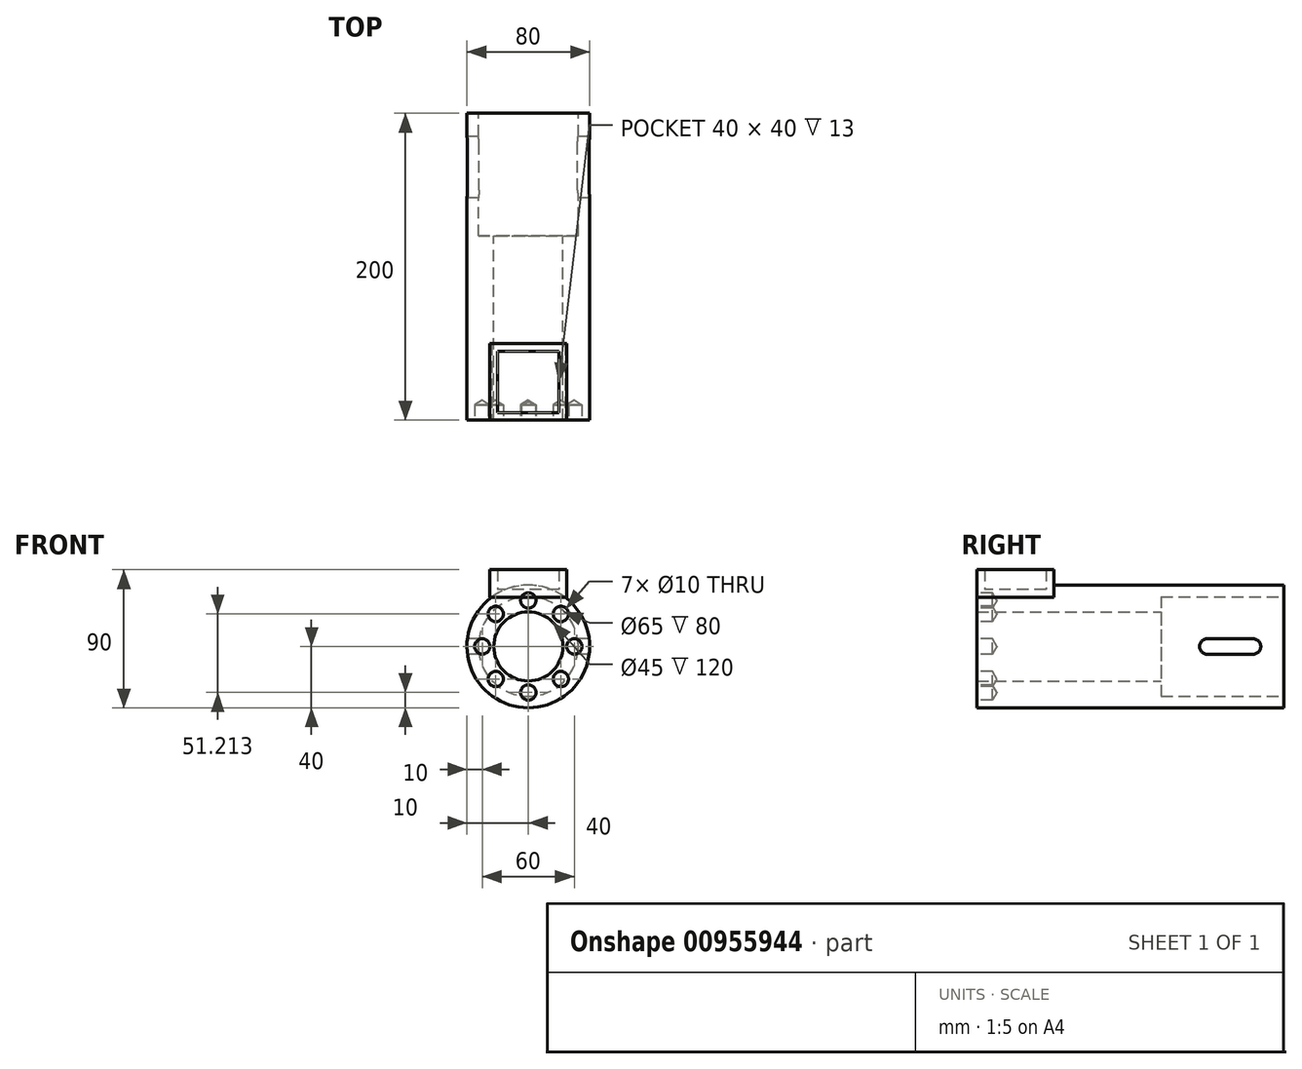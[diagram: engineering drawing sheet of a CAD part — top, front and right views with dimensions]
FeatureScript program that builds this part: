
annotation { "Feature Type Name" : "Feature", "Feature Type Description" : "" }
export const myFeature = defineFeature(function(context is Context, id is Id, definition is map)
    precondition{}
    {
        {
            var Q0;
            Q0=qCreatedBy(makeId("Front.planeOp"),FACE);
            var sketch = newSketch(context, id + "F0", { "sketchPlane" : qUnion([Q0])});
            skLineSegment(sketch, "E0", {"start": v(0, 0) * mm, "end": v(0, -32) * mm});
            skCircle(sketch, "E1", {"center": v(0, -32) * mm, "radius": 40 * mm});
            skSolve(sketch);
        }
        {
            var Q0;
            Q0=makeQuery(id+"F0.imprint","IMPRINT",FACE,{"disambiguationData":[TD([[makeQuery(id+"F0.imprint","IMPRINT",EDGE,{"derivedFrom":sQuery(id+"F0.wireOp",EDGE,"E1")}),1.0]])]});
            extrude(context, id + "F1", {"entities" : qUnion([Q0]), "oppositeDirection" : true, "depth" : 200 * mm, "offsetDistance" : 25 * mm});
        }
        {
            var Q0;
            Q0=qCreatedBy(makeId("Top.planeOp"),FACE);
            var sketch = newSketch(context, id + "F2", { "sketchPlane" : qUnion([Q0])});
            skLineSegment(sketch, "E2.bottom", {"start": v(25, 50) * mm, "end": v(-25, 50) * mm});
            skLineSegment(sketch, "E2.top", {"start": v(25, 0) * mm, "end": v(-25, 0) * mm});
            skLineSegment(sketch, "E2.left", {"start": v(25, 50) * mm, "end": v(25, 0) * mm});
            skLineSegment(sketch, "E2.right", {"start": v(-25, 50) * mm, "end": v(-25, 0) * mm});
            skPoint(sketch, "E2.middle", {"position": v(0, 25) * mm});
            skSolve(sketch);
        }
        {
            var Q0;
            Q0 = qSketchRegion(id + "F2", true);
            extrude(context, id + "F3", {"entities" : qUnion([Q0]), "operationType" : NewBodyOperationType.REMOVE, "depth" : 25 * mm, "offsetDistance" : 25 * mm});
        }
        {
            var Q0;
            Q0=makeQuery(id+"F2.imprint","IMPRINT",FACE,{"disambiguationData":[TD([[makeQuery(id+"F2.imprint","IMPRINT",EDGE,{"derivedFrom":sQuery(id+"F2.wireOp",EDGE,"E2.bottom")}),1.0]])]});
            extrude(context, id + "F4", {"entities" : qUnion([Q0]), "depth" : 18 * mm, "offsetDistance" : 25 * mm});
        }
        {
            var Q0;
            Q0=makeQuery(id+"F4.opExtrude","CAP_FACE",FACE,{"disambiguationData":[OSD([sQuery(id+"F2.wireOp",EDGE,"E2.bottom"),sQuery(id+"F2.wireOp",EDGE,"E2.top"),sQuery(id+"F2.wireOp",EDGE,"E2.left"),sQuery(id+"F2.wireOp",EDGE,"E2.right")])],"isStart":false});
            shell(context, id + "F5", {"entities" : qUnion([Q0]), "thickness" : 5 * mm});
        }
        {
            var Q0;
            Q0=makeQuery(id+"F1.opExtrude","CAP_FACE",FACE,{"disambiguationData":[OSD([sQuery(id+"F0.wireOp",EDGE,"E1")])],"isStart":false});
            var sketch = newSketch(context, id + "F6", { "sketchPlane" : qUnion([Q0])});
            skPoint(sketch, "E3", {"position": v(0, -32) * mm});
            skSolve(sketch);
        }
        {
            var Q0;
            Q0=sQuery(id+"F6.wireOp",VERTEX,"E3");
            var Q1;
            Q1=makeQuery(id+"F1.opExtrude","SWEPT_BODY",BODY,{"disambiguationData":[OSD([sQuery(id+"F0.wireOp",EDGE,"E1")])]});
            hole(context, id + "F7", {"style" : HoleStyle.C_BORE, "endStyle" : HoleEndStyle.THROUGH, "holeDiameter" : 45 * mm, "cBoreDiameter" : 65 * mm, "cBoreDepth" : 80 * mm, "majorDiameter" : 5 * mm, "isTappedThrough" : true, "tappedDepth" : 12 * mm, "tapClearance" : 3, "locations" : qUnion([Q0]), "scope" : qUnion([Q1])});
        }
        {
            var Q0;
            Q0=makeQuery(id+"F1.opExtrude","CAP_FACE",FACE,{"disambiguationData":[OSD([sQuery(id+"F0.wireOp",EDGE,"E1")])],"isStart":true});
            var sketch = newSketch(context, id + "F8", { "sketchPlane" : qUnion([Q0])});
            skLineSegment(sketch, "E4", {"start": v(0, -32) * mm, "end": v(30, -32) * mm});
            skLineSegment(sketch, "E5", {"start": v(0, -32) * mm, "end": v(0, -2) * mm});
            skLineSegment(sketch, "E6", {"start": v(0, -32) * mm, "end": v(-30, -32) * mm});
            skLineSegment(sketch, "E7", {"start": v(0, -32) * mm, "end": v(0, -62) * mm});
            skArc(sketch, "E8", {"start": v(0, -2) * mm, "mid": v(-21.21, -10.79) * mm, "end": v(-30, -32) * mm});
            skArc(sketch, "E9", {"start": v(-30, -32) * mm, "mid": v(-21.21, -53.21) * mm, "end": v(0, -62) * mm});
            skArc(sketch, "E10", {"start": v(0, -62) * mm, "mid": v(21.21, -53.21) * mm, "end": v(30, -32) * mm});
            skArc(sketch, "E11", {"start": v(30, -32) * mm, "mid": v(21.21, -10.79) * mm, "end": v(0, -2) * mm});
            skLineSegment(sketch, "E12", {"start": v(0, -32) * mm, "end": v(21.21, -10.79) * mm});
            skLineSegment(sketch, "E13", {"start": v(0, -32) * mm, "end": v(-21.21, -10.79) * mm});
            skLineSegment(sketch, "E14", {"start": v(0, -32) * mm, "end": v(-21.21, -53.21) * mm});
            skLineSegment(sketch, "E15", {"start": v(0, -32) * mm, "end": v(21.21, -53.21) * mm});
            skSolve(sketch);
        }
        {
            var Q0;
            Q0=sQuery(id+"F8.wireOp",VERTEX,"E12.end");
            var Q1;
            Q1=sQuery(id+"F8.wireOp",VERTEX,"E4.end");
            var Q2;
            Q2=sQuery(id+"F8.wireOp",VERTEX,"E15.end");
            var Q3;
            Q3=sQuery(id+"F8.wireOp",VERTEX,"E7.end");
            var Q4;
            Q4=sQuery(id+"F8.wireOp",VERTEX,"E14.end");
            var Q5;
            Q5=sQuery(id+"F8.wireOp",VERTEX,"E6.end");
            var Q6;
            Q6=sQuery(id+"F8.wireOp",VERTEX,"E13.end");
            var Q7;
            Q7=sQuery(id+"F8.wireOp",VERTEX,"E5.end");
            var Q8;
            Q8=makeQuery(id+"F1.opExtrude","SWEPT_BODY",BODY,{"disambiguationData":[OSD([sQuery(id+"F0.wireOp",EDGE,"E1")])]});
            var Q9;
            Q9=makeQuery(id+"F4.opExtrude","SWEPT_BODY",BODY,{"disambiguationData":[OSD([sQuery(id+"F2.wireOp",EDGE,"E2.bottom"),sQuery(id+"F2.wireOp",EDGE,"E2.top"),sQuery(id+"F2.wireOp",EDGE,"E2.left"),sQuery(id+"F2.wireOp",EDGE,"E2.right")])]});
            hole(context, id + "F9", {"style" : HoleStyle.SIMPLE, "endStyle" : HoleEndStyle.BLIND, "holeDiameter" : 10 * mm, "majorDiameter" : 5 * mm, "holeDepth" : 10 * mm, "isTappedThrough" : true, "tappedDepth" : 12 * mm, "tapClearance" : 3, "startFromSketch" : true, "locations" : qUnion([Q0, Q1, Q2, Q3, Q4, Q5, Q6, Q7]), "scope" : qUnion([Q8, Q9])});
        }
        {
            var Q0;
            Q0=qCreatedBy(makeId("Right.planeOp"),FACE);
            var sketch = newSketch(context, id + "F10", { "sketchPlane" : qUnion([Q0])});
            skLineSegment(sketch, "E16", {"start": v(0, -32) * mm, "end": v(217.32, -32) * mm});
            skLineSegment(sketch, "E17", {"start": v(0, 0) * mm, "end": v(251.66, 0) * mm});
            skSolve(sketch);
        }
        {
            var Q0;
            Q0=qCreatedBy(makeId("Right.planeOp"),FACE);
            var sketch = newSketch(context, id + "F11", { "sketchPlane" : qUnion([Q0])});
            skPoint(sketch, "E18.middle", {"position": v(0, 0) * mm});
            skLineSegment(sketch, "E19.bottom", {"start": v(150, -27) * mm, "end": v(180, -27) * mm});
            skLineSegment(sketch, "E19.top", {"start": v(150, -37) * mm, "end": v(180, -37) * mm});
            skLineSegment(sketch, "E19.left", {"start": v(145, -32) * mm, "end": v(145, -32) * mm});
            skLineSegment(sketch, "E19.right", {"start": v(185, -32) * mm, "end": v(185, -32) * mm});
            skPoint(sketch, "E20.visualSharp", {"position": v(185, -27) * mm});
            skArc(sketch, "E20.filletArc", {"start": v(185, -32) * mm, "mid": v(183.54, -28.46) * mm, "end": v(180, -27) * mm});
            skPoint(sketch, "E21.visualSharp", {"position": v(185, -37) * mm});
            skArc(sketch, "E21.filletArc", {"start": v(180, -37) * mm, "mid": v(183.54, -35.54) * mm, "end": v(185, -32) * mm});
            skPoint(sketch, "E22.visualSharp", {"position": v(145, -27) * mm});
            skArc(sketch, "E22.filletArc", {"start": v(150, -27) * mm, "mid": v(146.46, -28.46) * mm, "end": v(145, -32) * mm});
            skPoint(sketch, "E23.visualSharp", {"position": v(145, -37) * mm});
            skArc(sketch, "E23.filletArc", {"start": v(145, -32) * mm, "mid": v(146.46, -35.54) * mm, "end": v(150, -37) * mm});
            skSolve(sketch);
        }
        {
            var Q0;
            Q0 = qSketchRegion(id + "F11", true);
            extrude(context, id + "F12", {"entities" : qUnion([Q0]), "operationType" : NewBodyOperationType.REMOVE, "depth" : 100 * mm, "offsetDistance" : 25 * mm, "symmetric" : true});
        }
    });
